# Revit family: revitupgrade
name_source: partatom
category: Furniture
units: mm (PartAtom-declared; Revit-internal decimal feet)

## family parameters
Always vertical = Yes
Cut with Voids When Loaded = No
Enable Cutting in Views = No
OmniClass Number = 23.40.70.14.64.11
OmniClass Title = Office Furniture
Render Appearance Source = Family Geometry
Room Calculation Point = No
Shared = No
Work Plane-Based = No

## types (1)
- Module 5/6 - Left/Right Arm
    Assembly Code = E2020200
    Default Elevation = 0.00 mm
    Depth = 1000.00 mm
    Description = A lounge sofa concept with generous dimensions and timeless aesthetic. Based on traditional construction and layout, KITE provide a unique character through refined details and proportions.
    Height = 740.00 mm
    Leg Finish = Wendelbo_Wood_BlackStainedOak
    Manufacturer = Wendelbo
    Release Date = September 2021
    Style Number(s) = WBOKITEM5, WBOKITEM6
    URL = https://www.steelcase.com
    Width = 1680.00 mm

## geometry (parser evidence)
native form markers: Sweep x2
no freeform markers — native parametric forms only
